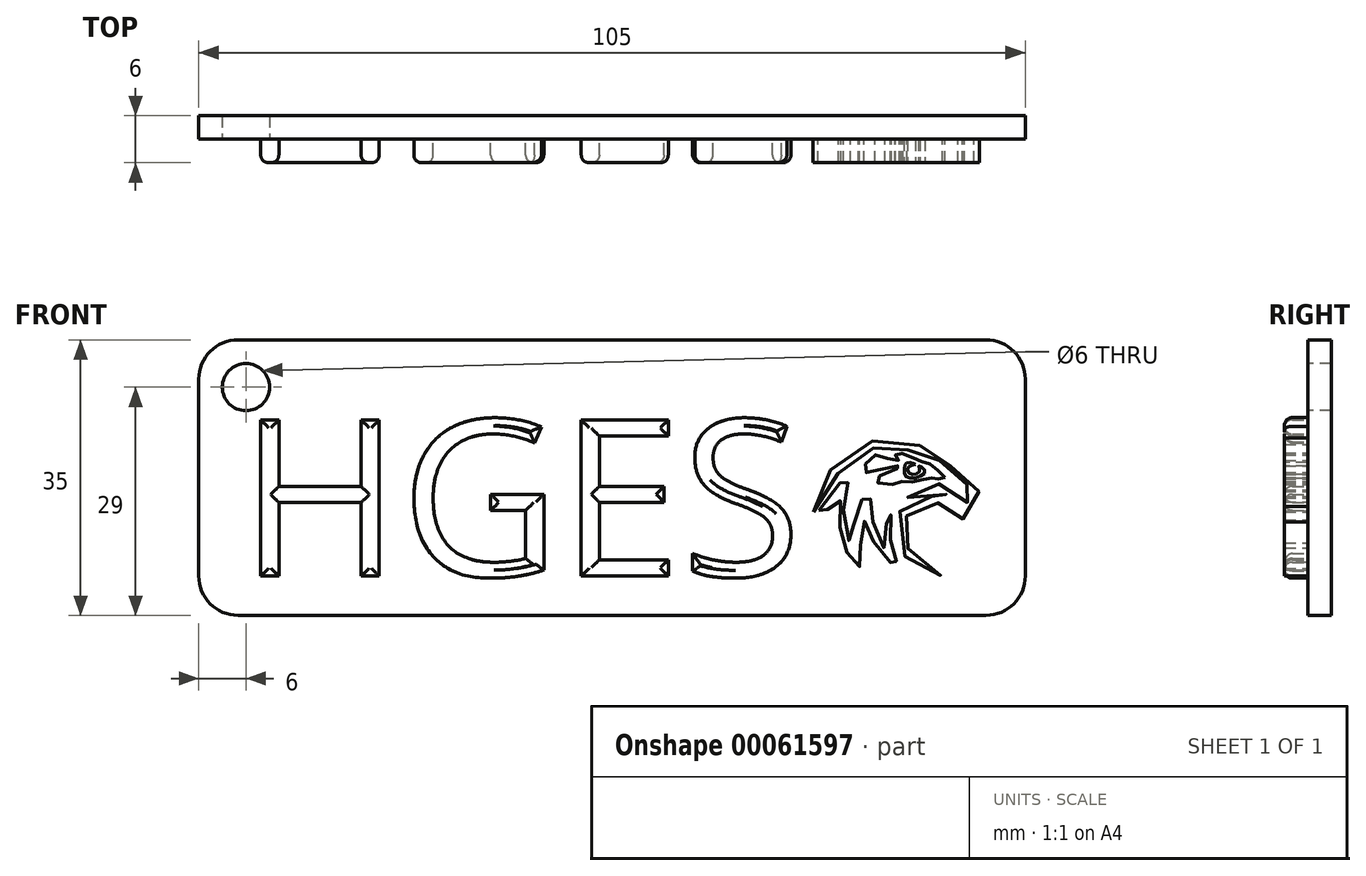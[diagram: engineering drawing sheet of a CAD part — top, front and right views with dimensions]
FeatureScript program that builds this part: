
annotation { "Feature Type Name" : "Feature", "Feature Type Description" : "" }
export const myFeature = defineFeature(function(context is Context, id is Id, definition is map)
    precondition{}
    {
        {
            var Q0;
            Q0=qCreatedBy(makeId("Front.planeOp"),FACE);
            var sketch = newSketch(context, id + "F0", { "sketchPlane" : qUnion([Q0])});
            skLineSegment(sketch, "E0.bottom", {"start": v(-55, 20) * mm, "end": v(50, 20) * mm});
            skLineSegment(sketch, "E0.top", {"start": v(-55, -15) * mm, "end": v(50, -15) * mm});
            skLineSegment(sketch, "E0.left", {"start": v(-55, 20) * mm, "end": v(-55, -15) * mm});
            skLineSegment(sketch, "E0.right", {"start": v(50, 20) * mm, "end": v(50, -15) * mm});
            skSolve(sketch);
        }
        {
            var Q0;
            Q0=makeQuery(id+"F0.imprint","IMPRINT",FACE,{"disambiguationData":[TD([[makeQuery(id+"F0.imprint","IMPRINT",EDGE,{"derivedFrom":sQuery(id+"F0.wireOp",EDGE,"E0.bottom")}),-1.0]])]});
            extrude(context, id + "F1", {"entities" : qUnion([Q0]), "oppositeDirection" : true, "depth" : 3 * mm});
        }
        {
            var Q0;
            Q0=makeQuery(id+"F1.opExtrude","CAP_FACE",FACE,{"disambiguationData":[OSD([sQuery(id+"F0.wireOp",EDGE,"E0.bottom"),sQuery(id+"F0.wireOp",EDGE,"E0.top"),sQuery(id+"F0.wireOp",EDGE,"E0.left"),sQuery(id+"F0.wireOp",EDGE,"E0.right")])],"isStart":true});
            var sketch = newSketch(context, id + "F2", { "sketchPlane" : qUnion([Q0])});
            skCircle(sketch, "E1", {"center": v(-49, 14) * mm, "radius": 3 * mm});
            skSolve(sketch);
        }
        {
            var Q0;
            Q0=qSketchRegion(id+"F2",true);
            extrude(context, id + "F3", {"entities" : qUnion([Q0]), "operationType" : NewBodyOperationType.REMOVE, "oppositeDirection" : true, "depth" : 6.35 * mm});
        }
        {
            var Q0;
            Q0=makeQuery(id+"F1.opExtrude","CAP_FACE",FACE,{"disambiguationData":[OSD([sQuery(id+"F0.wireOp",EDGE,"E0.bottom"),sQuery(id+"F0.wireOp",EDGE,"E0.top"),sQuery(id+"F0.wireOp",EDGE,"E0.left"),sQuery(id+"F0.wireOp",EDGE,"E0.right")])],"isStart":true});
            var sketch = newSketch(context, id + "F4", { "sketchPlane" : qUnion([Q0])});
            skText(sketch, "E2", { "text": "HGES", "fontName": "OpenSans-Regular.ttf"});
            const initialGuessF4  = {"E2": [-0.04985, -0.01, 1, 0, 0.02]};
            skSetInitialGuess(sketch, initialGuessF4);
            skSolve(sketch);
        }
        {
            var Q0;
            Q0=qSketchRegion(id+"F4",true);
            extrude(context, id + "F5", {"entities" : qUnion([Q0]), "operationType" : NewBodyOperationType.ADD, "depth" : 3 * mm});
        }
        {
            var Q0;
            Q0=makeQuery(id+"F5.opExtrude","CAP_FACE",FACE,{"disambiguationData":[OSD([sQuery(id+"F4.wireOp",EDGE,"E2.sketch_text.stroke-0"),sQuery(id+"F4.wireOp",EDGE,"E2.sketch_text.stroke-1"),sQuery(id+"F4.wireOp",EDGE,"E2.sketch_text.stroke-2"),sQuery(id+"F4.wireOp",EDGE,"E2.sketch_text.stroke-3"),sQuery(id+"F4.wireOp",EDGE,"E2.sketch_text.stroke-4"),sQuery(id+"F4.wireOp",EDGE,"E2.sketch_text.stroke-5"),sQuery(id+"F4.wireOp",EDGE,"E2.sketch_text.stroke-6"),sQuery(id+"F4.wireOp",EDGE,"E2.sketch_text.stroke-7"),sQuery(id+"F4.wireOp",EDGE,"E2.sketch_text.stroke-8"),sQuery(id+"F4.wireOp",EDGE,"E2.sketch_text.stroke-9"),sQuery(id+"F4.wireOp",EDGE,"E2.sketch_text.stroke-10"),sQuery(id+"F4.wireOp",EDGE,"E2.sketch_text.stroke-11")])],"isStart":false});
            var Q1;
            Q1=makeQuery(id+"F5.opExtrude","CAP_FACE",FACE,{"disambiguationData":[OSD([sQuery(id+"F4.wireOp",EDGE,"E2.sketch_text.stroke-12"),sQuery(id+"F4.wireOp",EDGE,"E2.sketch_text.stroke-13"),sQuery(id+"F4.wireOp",EDGE,"E2.sketch_text.stroke-14"),sQuery(id+"F4.wireOp",EDGE,"E2.sketch_text.stroke-15"),sQuery(id+"F4.wireOp",EDGE,"E2.sketch_text.stroke-16"),sQuery(id+"F4.wireOp",EDGE,"E2.sketch_text.stroke-17"),sQuery(id+"F4.wireOp",EDGE,"E2.sketch_text.stroke-18"),sQuery(id+"F4.wireOp",EDGE,"E2.sketch_text.stroke-19"),sQuery(id+"F4.wireOp",EDGE,"E2.sketch_text.stroke-20"),sQuery(id+"F4.wireOp",EDGE,"E2.sketch_text.stroke-21"),sQuery(id+"F4.wireOp",EDGE,"E2.sketch_text.stroke-22"),sQuery(id+"F4.wireOp",EDGE,"E2.sketch_text.stroke-23"),sQuery(id+"F4.wireOp",EDGE,"E2.sketch_text.stroke-24"),sQuery(id+"F4.wireOp",EDGE,"E2.sketch_text.stroke-25"),sQuery(id+"F4.wireOp",EDGE,"E2.sketch_text.stroke-26"),sQuery(id+"F4.wireOp",EDGE,"E2.sketch_text.stroke-27"),sQuery(id+"F4.wireOp",EDGE,"E2.sketch_text.stroke-28"),sQuery(id+"F4.wireOp",EDGE,"E2.sketch_text.stroke-29"),sQuery(id+"F4.wireOp",EDGE,"E2.sketch_text.stroke-30"),sQuery(id+"F4.wireOp",EDGE,"E2.sketch_text.stroke-31")])],"isStart":false});
            var Q2;
            Q2=makeQuery(id+"F5.opExtrude","CAP_FACE",FACE,{"disambiguationData":[OSD([sQuery(id+"F4.wireOp",EDGE,"E2.sketch_text.stroke-32"),sQuery(id+"F4.wireOp",EDGE,"E2.sketch_text.stroke-33"),sQuery(id+"F4.wireOp",EDGE,"E2.sketch_text.stroke-34"),sQuery(id+"F4.wireOp",EDGE,"E2.sketch_text.stroke-35"),sQuery(id+"F4.wireOp",EDGE,"E2.sketch_text.stroke-36"),sQuery(id+"F4.wireOp",EDGE,"E2.sketch_text.stroke-37"),sQuery(id+"F4.wireOp",EDGE,"E2.sketch_text.stroke-38"),sQuery(id+"F4.wireOp",EDGE,"E2.sketch_text.stroke-39"),sQuery(id+"F4.wireOp",EDGE,"E2.sketch_text.stroke-40"),sQuery(id+"F4.wireOp",EDGE,"E2.sketch_text.stroke-41"),sQuery(id+"F4.wireOp",EDGE,"E2.sketch_text.stroke-42"),sQuery(id+"F4.wireOp",EDGE,"E2.sketch_text.stroke-43")])],"isStart":false});
            var Q3;
            Q3=makeQuery(id+"F5.opExtrude","CAP_FACE",FACE,{"disambiguationData":[OSD([sQuery(id+"F4.wireOp",EDGE,"E2.sketch_text.stroke-44"),sQuery(id+"F4.wireOp",EDGE,"E2.sketch_text.stroke-45"),sQuery(id+"F4.wireOp",EDGE,"E2.sketch_text.stroke-46"),sQuery(id+"F4.wireOp",EDGE,"E2.sketch_text.stroke-47"),sQuery(id+"F4.wireOp",EDGE,"E2.sketch_text.stroke-48"),sQuery(id+"F4.wireOp",EDGE,"E2.sketch_text.stroke-49"),sQuery(id+"F4.wireOp",EDGE,"E2.sketch_text.stroke-50"),sQuery(id+"F4.wireOp",EDGE,"E2.sketch_text.stroke-51"),sQuery(id+"F4.wireOp",EDGE,"E2.sketch_text.stroke-52"),sQuery(id+"F4.wireOp",EDGE,"E2.sketch_text.stroke-53"),sQuery(id+"F4.wireOp",EDGE,"E2.sketch_text.stroke-54"),sQuery(id+"F4.wireOp",EDGE,"E2.sketch_text.stroke-55"),sQuery(id+"F4.wireOp",EDGE,"E2.sketch_text.stroke-56"),sQuery(id+"F4.wireOp",EDGE,"E2.sketch_text.stroke-57"),sQuery(id+"F4.wireOp",EDGE,"E2.sketch_text.stroke-58"),sQuery(id+"F4.wireOp",EDGE,"E2.sketch_text.stroke-59"),sQuery(id+"F4.wireOp",EDGE,"E2.sketch_text.stroke-60"),sQuery(id+"F4.wireOp",EDGE,"E2.sketch_text.stroke-61"),sQuery(id+"F4.wireOp",EDGE,"E2.sketch_text.stroke-62"),sQuery(id+"F4.wireOp",EDGE,"E2.sketch_text.stroke-63"),sQuery(id+"F4.wireOp",EDGE,"E2.sketch_text.stroke-64"),sQuery(id+"F4.wireOp",EDGE,"E2.sketch_text.stroke-65"),sQuery(id+"F4.wireOp",EDGE,"E2.sketch_text.stroke-66"),sQuery(id+"F4.wireOp",EDGE,"E2.sketch_text.stroke-67"),sQuery(id+"F4.wireOp",EDGE,"E2.sketch_text.stroke-68")])],"isStart":false});
            fillet(context, id + "F6", {"entities" : qUnion([Q0, Q1, Q2, Q3]), "radius" : 1 * mm, "tangentPropagation" : true, "allowEdgeOverflow" : false});
        }
        {
            var Q0;
            Q0=makeQuery(id+"F1.opExtrude","CAP_FACE",FACE,{"disambiguationData":[OSD([sQuery(id+"F0.wireOp",EDGE,"E0.bottom"),sQuery(id+"F0.wireOp",EDGE,"E0.top"),sQuery(id+"F0.wireOp",EDGE,"E0.left"),sQuery(id+"F0.wireOp",EDGE,"E0.right")])],"isStart":true});
            var sketch = newSketch(context, id + "F7", { "sketchPlane" : qUnion([Q0])});
            skFitSpline(sketch, "E3", {"points": [v(23.82, -1.68) * mm, v(26, 1.34) * mm, v(27.75, 2.92) * mm, v(27.33, 1.5) * mm, v(26.91, -1) * mm, v(27.24, -3.93) * mm, v(27.75, -5.77) * mm, v(28.08, -4.35) * mm, v(28.67, -1.76) * mm, v(29.42, 0) * mm, v(30.09, 0.92) * mm, v(30.34, -0.92) * mm, v(30.5, -2.43) * mm, v(31.1, -4.52) * mm, v(32.1, -6.44) * mm, v(32.18, -4.27) * mm, v(32.6, -2.43) * mm, v(32.76, -1.76) * mm, v(33.02, -2.93) * mm, v(32.85, -5.02) * mm, v(33.1, -6.61) * mm, v(33.6, -8.12) * mm, v(34.02, -9.2) * mm, v(32.68, -8.12) * mm, v(31.1, -6.28) * mm, v(30.09, -4.18) * mm, v(29.59, -3.01) * mm, v(29.08, -4.6) * mm, v(29, -6.53) * mm, v(28.83, -7.86) * mm, v(28.92, -9.04) * mm, v(27.75, -7.78) * mm, v(26.91, -5.86) * mm, v(26.4, -3.43) * mm, v(26.33, -1) * mm, v(26.58, 0) * mm, v(25.49, -0.76) * mm, v(23.82, -2.85) * mm, v(23.82, -1.68) * mm]});
            skSolve(sketch);
        }
        {
            var Q0;
            Q0=qSketchRegion(id+"F7",true);
            extrude(context, id + "F8", {"entities" : qUnion([Q0]), "operationType" : NewBodyOperationType.ADD, "depth" : 3 * mm});
        }
        {
            var Q0;
            Q0=makeQuery(id+"F1.opExtrude","CAP_FACE",FACE,{"disambiguationData":[OSD([sQuery(id+"F0.wireOp",EDGE,"E0.bottom"),sQuery(id+"F0.wireOp",EDGE,"E0.top"),sQuery(id+"F0.wireOp",EDGE,"E0.left"),sQuery(id+"F0.wireOp",EDGE,"E0.right")])],"isStart":true});
            var sketch = newSketch(context, id + "F9", { "sketchPlane" : qUnion([Q0])});
            skFitSpline(sketch, "E4", {"points": [v(23.1, -1.86) * mm, v(23.81, 0.98) * mm, v(25.7, 3.98) * mm, v(28.86, 6.43) * mm, v(33.05, 7.54) * mm, v(36.28, 6.67) * mm, v(39.13, 5.8) * mm, v(40.23, 4.23) * mm, v(41.97, 3.12) * mm, v(43.79, 1.46) * mm, v(43.87, -1.22) * mm, v(42.05, -3.11) * mm, v(42.3, -1.77) * mm, v(40.95, -0.83) * mm, v(38.5, -0.67) * mm, v(37.08, -0.67) * mm, v(35.03, -2.25) * mm, v(34.48, -3.83) * mm, v(34.63, -5.33) * mm, v(36.21, -7.85) * mm, v(39.45, -9.75) * mm, v(37.87, -9.9) * mm, v(35.43, -8.33) * mm, v(33.84, -5.96) * mm, v(33.84, -2.1) * mm, v(35.74, -0.6) * mm, v(37, 0) * mm, v(39.84, 0) * mm, v(41.42, 0) * mm, v(37.54, 0.73) * mm, v(35.86, 0.49) * mm, v(35.02, 0) * mm, v(35.55, 1.01) * mm, v(38.46, 1.74) * mm, v(40.54, 1.44) * mm, v(42.25, 0.55) * mm, v(42.92, -1.14) * mm, v(43.47, 0) * mm, v(42.92, 1.39) * mm, v(40.7, 2.88) * mm, v(39.29, 4.23) * mm, v(38.9, 5.02) * mm, v(37.4, 5.49) * mm, v(35.02, 6.04) * mm, v(33.36, 6.67) * mm, v(31.39, 6.43) * mm, v(28.78, 5.4) * mm, v(26.42, 3.2) * mm, v(25.15, 1.7) * mm, v(23.1, -1.86) * mm]});
            skSolve(sketch);
        }
        {
            var Q0;
            Q0=qSketchRegion(id+"F9",true);
            extrude(context, id + "F10", {"entities" : qUnion([Q0]), "operationType" : NewBodyOperationType.ADD, "depth" : 3 * mm});
        }
        {
            var Q0;
            Q0=makeQuery(id+"F1.opExtrude","CAP_FACE",FACE,{"disambiguationData":[OSD([sQuery(id+"F0.wireOp",EDGE,"E0.bottom"),sQuery(id+"F0.wireOp",EDGE,"E0.top"),sQuery(id+"F0.wireOp",EDGE,"E0.left"),sQuery(id+"F0.wireOp",EDGE,"E0.right")])],"isStart":true});
            var sketch = newSketch(context, id + "F11", { "sketchPlane" : qUnion([Q0])});
            skFitSpline(sketch, "E5", {"points": [v(39.76, 2.54) * mm, v(39.1, 2.36) * mm, v(38.4, 2.36) * mm, v(37.87, 2.49) * mm, v(36.1, 2) * mm, v(34.4, 2) * mm, v(33.02, 1.62) * mm, v(30.9, 2.21) * mm, v(34.18, 3.9) * mm, v(32.13, 3.7) * mm, v(29.55, 3.3) * mm, v(30.65, 5.3) * mm, v(32.97, 4.78) * mm, v(33.99, 4.8) * mm, v(33.44, 5.49) * mm, v(35.02, 5.4) * mm, v(36.4, 4.67) * mm, v(37.56, 4.4) * mm, v(38.58, 3.67) * mm, v(39.76, 2.54) * mm]});
            skSolve(sketch);
        }
        {
            var Q0;
            Q0=qSketchRegion(id+"F11",true);
            extrude(context, id + "F12", {"entities" : qUnion([Q0]), "operationType" : NewBodyOperationType.ADD, "depth" : 3 * mm});
        }
        {
            var Q0;
            Q0=makeQuery(id+"F12.opExtrude","CAP_FACE",FACE,{"disambiguationData":[OSD([sQuery(id+"F11.wireOp",EDGE,"E5")])],"isStart":false});
            var sketch = newSketch(context, id + "F13", { "sketchPlane" : qUnion([Q0])});
            skFitSpline(sketch, "E6", {"points": [v(36.02, 4.2) * mm, v(35.66, 4.34) * mm, v(34.89, 4.34) * mm, v(34.65, 3.77) * mm, v(34.83, 2.62) * mm, v(36.6, 2.65) * mm, v(37.22, 3.46) * mm, v(36.47, 3.96) * mm, v(36.6, 3.54) * mm, v(36.01, 2.94) * mm, v(35.12, 3.2) * mm, v(35.31, 4) * mm, v(36.02, 4.2) * mm]});
            skSolve(sketch);
        }
        {
            var Q0;
            Q0=qSketchRegion(id+"F13",true);
            extrude(context, id + "F14", {"entities" : qUnion([Q0]), "operationType" : NewBodyOperationType.REMOVE, "oppositeDirection" : true, "depth" : 3 * mm});
        }
        {
            var Q0;
            Q0=makeQuery(id+"F1.opExtrude","SWEPT_EDGE",EDGE,{"disambiguationData":[OSD([sQuery(id+"F0.wireOp",EDGE,"E0.bottom"),sQuery(id+"F0.wireOp",EDGE,"E0.left")])]});
            var Q1;
            Q1=makeQuery(id+"F1.opExtrude","SWEPT_EDGE",EDGE,{"disambiguationData":[OSD([sQuery(id+"F0.wireOp",EDGE,"E0.top"),sQuery(id+"F0.wireOp",EDGE,"E0.right")])]});
            var Q2;
            Q2=makeQuery(id+"F1.opExtrude","SWEPT_EDGE",EDGE,{"disambiguationData":[OSD([sQuery(id+"F0.wireOp",EDGE,"E0.bottom"),sQuery(id+"F0.wireOp",EDGE,"E0.right")])]});
            var Q3;
            Q3=makeQuery(id+"F1.opExtrude","SWEPT_EDGE",EDGE,{"disambiguationData":[OSD([sQuery(id+"F0.wireOp",EDGE,"E0.top"),sQuery(id+"F0.wireOp",EDGE,"E0.left")])]});
            fillet(context, id + "F15", {"entities" : qUnion([Q0, Q1, Q2, Q3]), "radius" : 5 * mm, "tangentPropagation" : true, "allowEdgeOverflow" : false});
        }
    });
